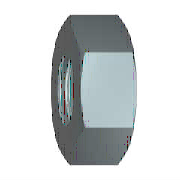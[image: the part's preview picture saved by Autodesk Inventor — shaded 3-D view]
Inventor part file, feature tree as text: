
AUTODESK INVENTOR PART (.ipt)
format: ipt  version: 2015 (Build 190159000, 159)  size: 173,568 bytes
history: native  units: mm (DEFAULTED — no unit token found)
features: sketch x3, chamfer x1, hole x1, other x1, plane x1
ambient origin geometry x7: Origin, YZ Plane, XZ Plane, X Axis, Y Axis, Z Axis, Center Point
bodies: Solid1 (feature_tree), Body (feature_tree)
feature tree (7):
  chamfer  "Chamfer1"  Distance=4.363323mm
  hole  "Thread"  [1 undecoded]
  other  "Work Axis1"
  plane  "Work Plane1"
  sketch  "Sketch1"  dims[d0=6.928203mm]
  sketch  "Sketch2"  dims[d1=2.8mm]
  sketch  "Sketch3"  dims[d2=0.0mm d3=4.363323mm d4=4.363323mm d5=6.0mm d6=6.0mm d7=90.0deg d25=2.85mm d26=6.0mm d27=4.0mm d28=2.0mm d29=14.3117mm d30=8.0mm d31=20.594885mm d8=0.32476mm d9=30.0deg d10=0.32476mm d11=30.0deg d13=0.0mm d14=0.0mm d39=0.0mm d40=0.32476mm d41=0.32476mm d42=0.0mm]
note: 1 required parameter value undecoded (feature->parameter linkage not recoverable at this tier; creation-order binding heuristic only, values carry confidence <= 0.55)
